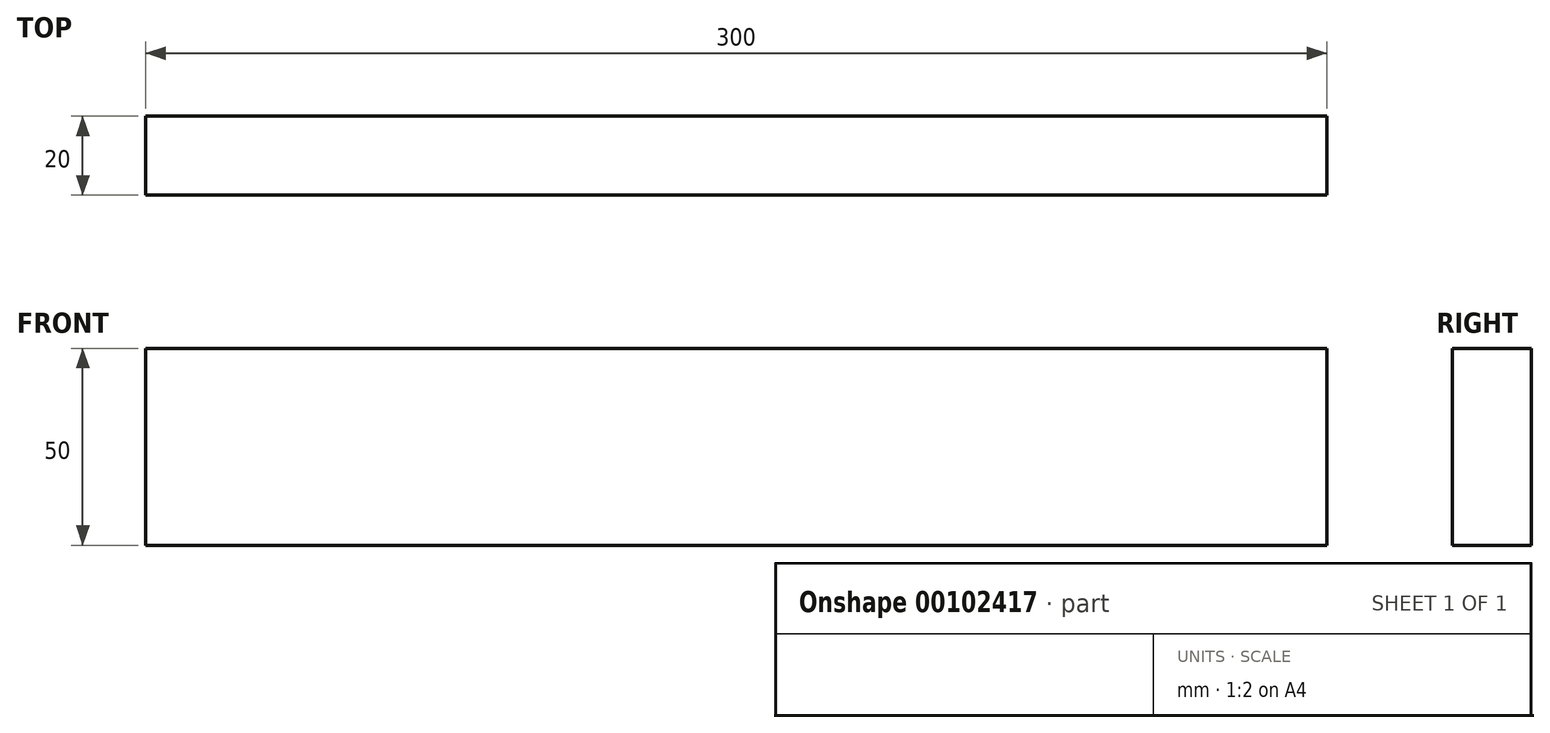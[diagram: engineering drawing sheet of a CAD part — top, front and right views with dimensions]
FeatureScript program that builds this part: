
annotation { "Feature Type Name" : "Feature", "Feature Type Description" : "" }
export const myFeature = defineFeature(function(context is Context, id is Id, definition is map)
    precondition{}
    {
        {
            var Q0;
            Q0=qCreatedBy(makeId("Front.planeOp"),FACE);
            var sketch = newSketch(context, id + "F0", { "sketchPlane" : qUnion([Q0])});
            skLineSegment(sketch, "E0.bottom", {"start": v(0, 0) * mm, "end": v(300, 0) * mm});
            skLineSegment(sketch, "E0.top", {"start": v(0, 50) * mm, "end": v(300, 50) * mm});
            skLineSegment(sketch, "E0.left", {"start": v(0, 0) * mm, "end": v(0, 50) * mm});
            skLineSegment(sketch, "E0.right", {"start": v(300, 0) * mm, "end": v(300, 50) * mm});
            skSolve(sketch);
        }
        {
            var Q0;
            Q0=makeQuery(id+"F0.imprint","IMPRINT",FACE,{"disambiguationData":[TD([[makeQuery(id+"F0.imprint","IMPRINT",EDGE,{"derivedFrom":sQuery(id+"F0.wireOp",EDGE,"E0.bottom")}),1.0]])]});
            extrude(context, id + "F1", {"entities" : qUnion([Q0]), "depth" : 20 * mm});
        }
    });
